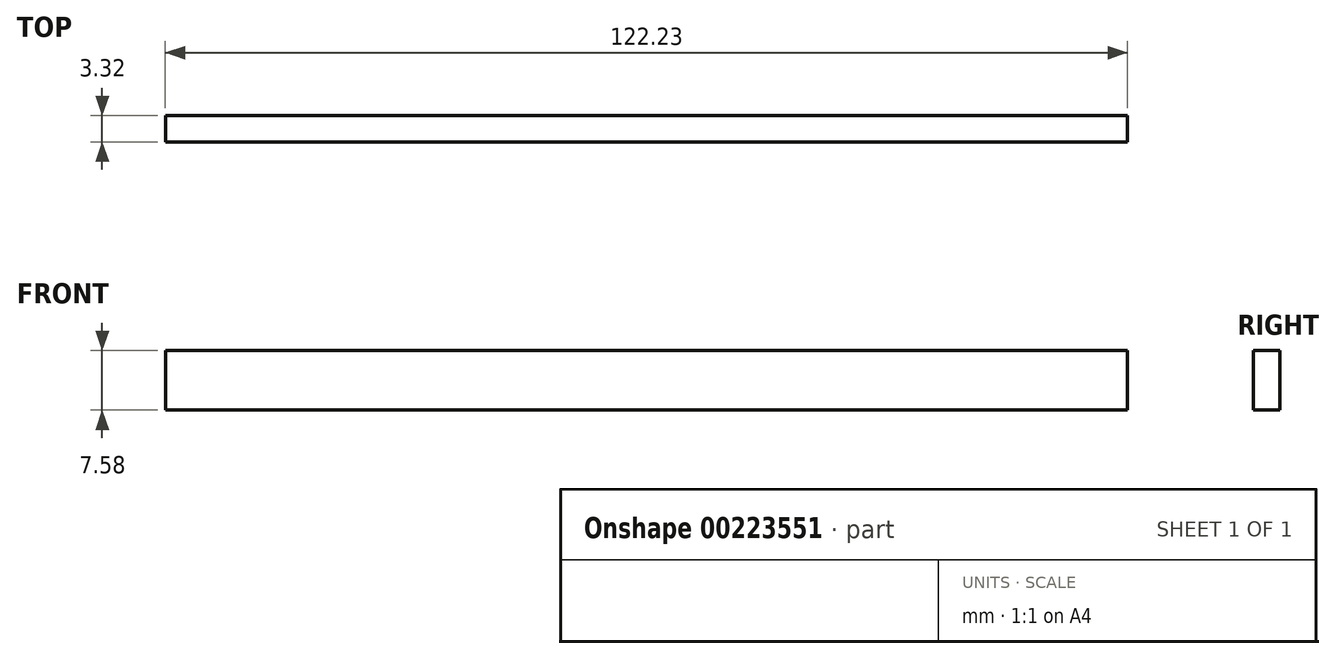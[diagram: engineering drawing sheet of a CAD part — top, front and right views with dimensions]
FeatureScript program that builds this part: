
annotation { "Feature Type Name" : "Feature", "Feature Type Description" : "" }
export const myFeature = defineFeature(function(context is Context, id is Id, definition is map)
    precondition{}
    {
        {
            var Q0;
            Q0=qCreatedBy(makeId("Top.planeOp"),FACE);
            var sketch = newSketch(context, id + "F0", { "sketchPlane" : qUnion([Q0])});
            skLineSegment(sketch, "E0.bottom", {"start": v(53.28, 21.77) * mm, "end": v(-68.95, 21.77) * mm});
            skLineSegment(sketch, "E0.top", {"start": v(53.28, 18.45) * mm, "end": v(-68.95, 18.45) * mm});
            skLineSegment(sketch, "E0.left", {"start": v(53.28, 21.77) * mm, "end": v(53.28, 18.45) * mm});
            skLineSegment(sketch, "E0.right", {"start": v(-68.95, 21.77) * mm, "end": v(-68.95, 18.45) * mm});
            skSolve(sketch);
        }
        {
            var Q0;
            Q0=makeQuery(id+"F0.imprint","IMPRINT",FACE,{"disambiguationData":[TD([[makeQuery(id+"F0.imprint","IMPRINT",EDGE,{"derivedFrom":sQuery(id+"F0.wireOp",EDGE,"E0.bottom")}),1.0]])]});
            extrude(context, id + "F1", {"entities" : qUnion([Q0]), "depth" : 25.4 * mm});
        }
        {
            var Q0;
            Q0=makeQuery(id+"F1.opExtrude","CAP_FACE",FACE,{"disambiguationData":[OSD([sQuery(id+"F0.wireOp",EDGE,"E0.bottom"),sQuery(id+"F0.wireOp",EDGE,"E0.top"),sQuery(id+"F0.wireOp",EDGE,"E0.left"),sQuery(id+"F0.wireOp",EDGE,"E0.right")])],"isStart":false});
            extrude(context, id + "F3", {"entities" : qUnion([Q0]), "operationType" : NewBodyOperationType.REMOVE, "oppositeDirection" : true, "depth" : 17.82 * mm});
        }
    });
